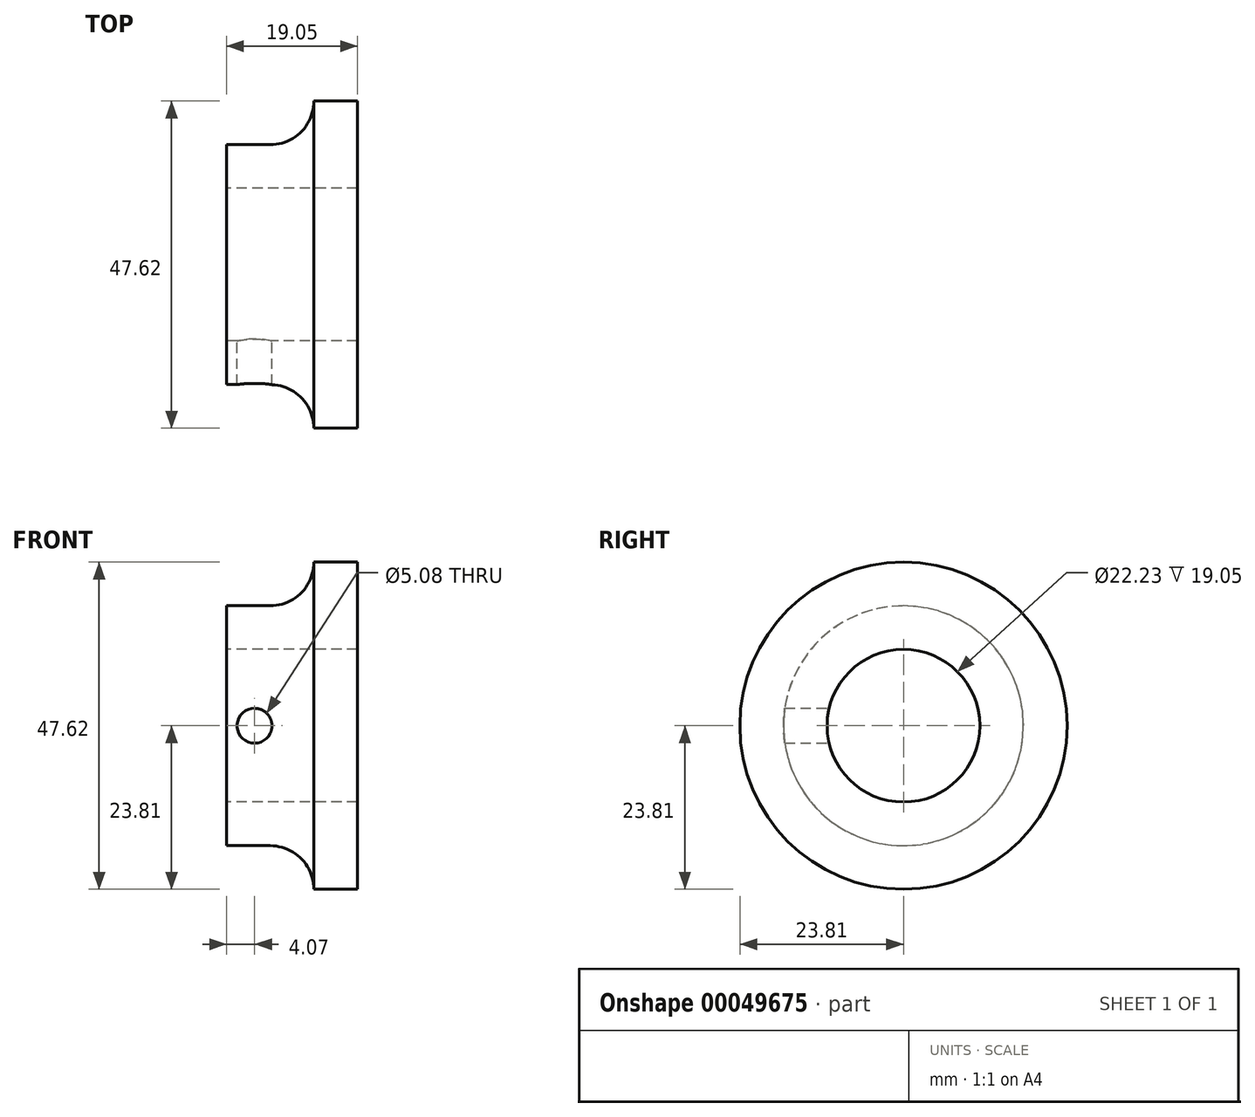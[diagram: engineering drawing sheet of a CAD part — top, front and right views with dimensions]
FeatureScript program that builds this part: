
annotation { "Feature Type Name" : "Feature", "Feature Type Description" : "" }
export const myFeature = defineFeature(function(context is Context, id is Id, definition is map)
    precondition{}
    {
        {
            var Q0;
            Q0=qCreatedBy(makeId("Front.planeOp"),FACE);
            var sketch = newSketch(context, id + "F0", { "sketchPlane" : qUnion([Q0])});
            skLineSegment(sketch, "E0", {"start": v(-38.46, 0) * mm, "end": v(43.13, 0) * mm, "construction": true});
            skLineSegment(sketch, "E1", {"start": v(-11.7, 11.11) * mm, "end": v(7.36, 11.11) * mm});
            skLineSegment(sketch, "E2", {"start": v(7.36, 11.11) * mm, "end": v(7.36, 23.81) * mm});
            skLineSegment(sketch, "E3", {"start": v(-11.7, 11.11) * mm, "end": v(-11.7, 17.46) * mm});
            skLineSegment(sketch, "E4", {"start": v(7.36, 23.81) * mm, "end": v(1, 23.81) * mm});
            skLineSegment(sketch, "E5", {"start": v(-11.7, 17.46) * mm, "end": v(-5.34, 17.46) * mm});
            skArc(sketch, "E6", {"start": v(-5.34, 17.46) * mm, "mid": v(-0.85, 19.32) * mm, "end": v(1, 23.81) * mm});
            skSolve(sketch);
        }
        {
            var Q0;
            Q0 = qSketchRegion(id + "F0", true);
            var Q1;
            Q1=sQuery(id+"F0.wireOp",EDGE,"E0");
            revolve(context, id + "F1", {"entities" : qUnion([Q0]), "axis" : qUnion([Q1]), "revolveType" : RevolveType.FULL});
        }
        {
            var Q0;
            Q0=qCreatedBy(makeId("Front.planeOp"),FACE);
            var sketch = newSketch(context, id + "F2", { "sketchPlane" : qUnion([Q0])});
            skCircle(sketch, "E7", {"center": v(-7.62, 0) * mm, "radius": 2.54 * mm});
            skSolve(sketch);
        }
        {
            var Q0;
            Q0=makeQuery(id+"F2.imprint","IMPRINT",FACE,{"disambiguationData":[TD([[makeQuery(id+"F2.imprint","IMPRINT",EDGE,{"derivedFrom":sQuery(id+"F2.wireOp",EDGE,"E7")}),1.0]])]});
            extrude(context, id + "F3", {"entities" : qUnion([Q0]), "operationType" : NewBodyOperationType.REMOVE, "depth" : 25.4 * mm});
        }
    });
